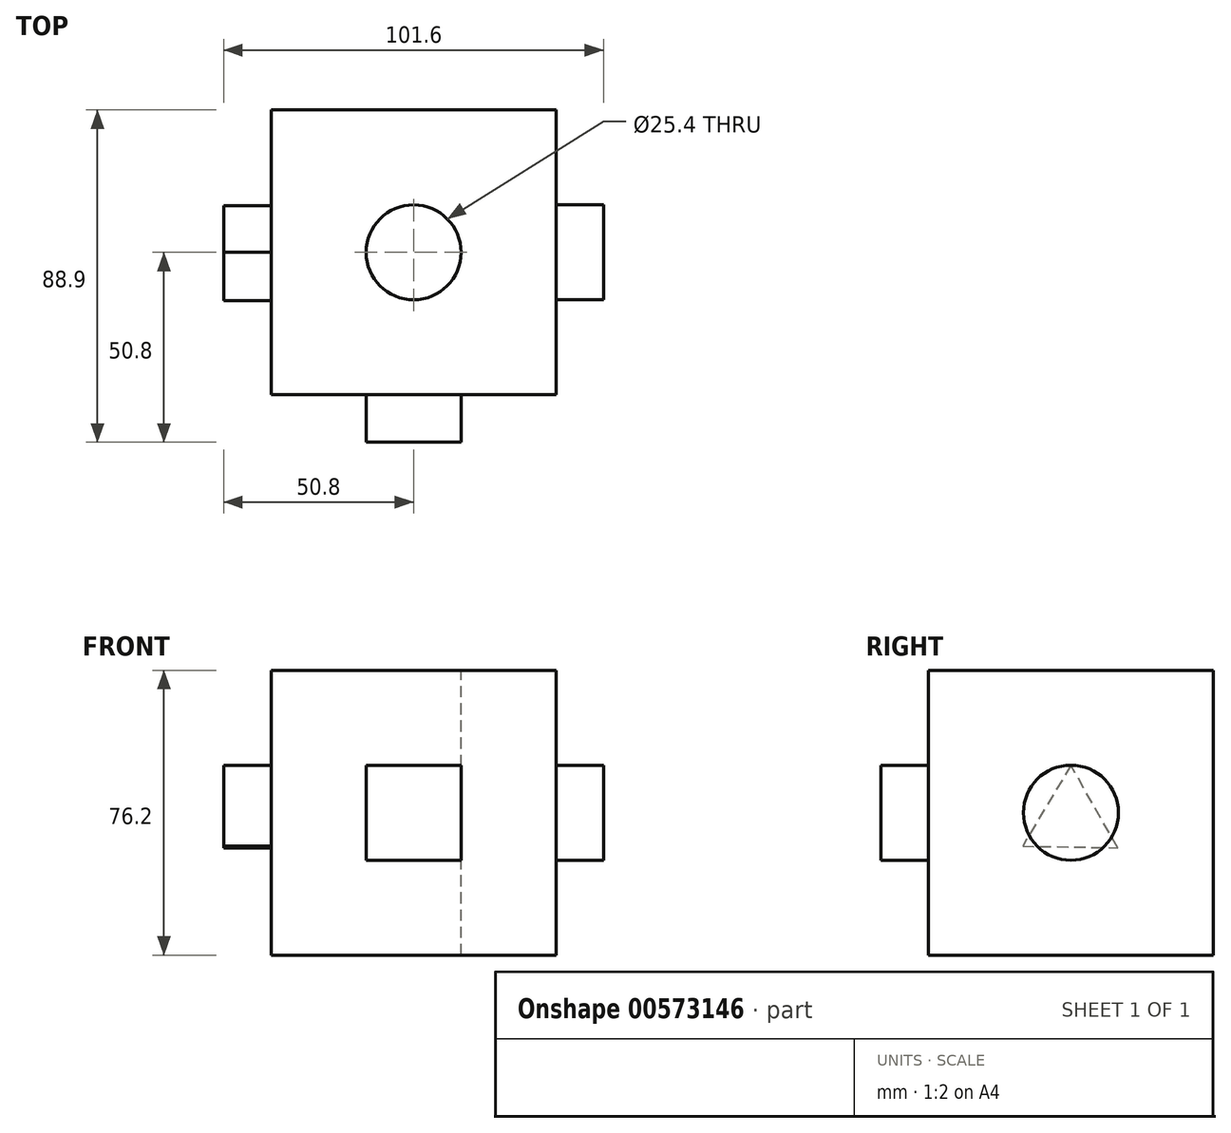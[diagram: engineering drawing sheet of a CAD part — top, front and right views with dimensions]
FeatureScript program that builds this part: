
annotation { "Feature Type Name" : "Feature", "Feature Type Description" : "" }
export const myFeature = defineFeature(function(context is Context, id is Id, definition is map)
    precondition{}
    {
        {
            var Q0;
            Q0=qCreatedBy(makeId("Front.planeOp"),FACE);
            var sketch = newSketch(context, id + "F0", { "sketchPlane" : qUnion([Q0])});
            skLineSegment(sketch, "E0.bottom", {"start": v(0, 0) * mm, "end": v(-76.2, 0) * mm});
            skLineSegment(sketch, "E0.top", {"start": v(0, 76.2) * mm, "end": v(-76.2, 76.2) * mm});
            skLineSegment(sketch, "E0.left", {"start": v(0, 0) * mm, "end": v(0, 76.2) * mm});
            skLineSegment(sketch, "E0.right", {"start": v(-76.2, 0) * mm, "end": v(-76.2, 76.2) * mm});
            skSolve(sketch);
        }
        {
            var Q0;
            Q0=makeQuery(id+"F0.imprint","IMPRINT",FACE,{"disambiguationData":[TD([[makeQuery(id+"F0.imprint","IMPRINT",EDGE,{"derivedFrom":sQuery(id+"F0.wireOp",EDGE,"E0.bottom")}),-1.0]])]});
            extrude(context, id + "F1", {"entities" : qUnion([Q0]), "depth" : 76.2 * mm, "offsetDistance" : 25.4 * mm});
        }
        {
            var Q0;
            Q0=makeQuery(id+"F1.opExtrude","CAP_FACE",FACE,{"disambiguationData":[OSD([sQuery(id+"F0.wireOp",EDGE,"E0.bottom"),sQuery(id+"F0.wireOp",EDGE,"E0.top"),sQuery(id+"F0.wireOp",EDGE,"E0.left"),sQuery(id+"F0.wireOp",EDGE,"E0.right")])],"isStart":false});
            var sketch = newSketch(context, id + "F2", { "sketchPlane" : qUnion([Q0])});
            skLineSegment(sketch, "E1.bottom", {"start": v(-50.8, 50.8) * mm, "end": v(-25.4, 50.8) * mm});
            skLineSegment(sketch, "E1.top", {"start": v(-50.8, 25.4) * mm, "end": v(-25.4, 25.4) * mm});
            skLineSegment(sketch, "E1.left", {"start": v(-50.8, 50.8) * mm, "end": v(-50.8, 25.4) * mm});
            skLineSegment(sketch, "E1.right", {"start": v(-25.4, 50.8) * mm, "end": v(-25.4, 25.4) * mm});
            skSolve(sketch);
        }
        {
            var Q0;
            Q0=makeQuery(id+"F2.imprint","IMPRINT",FACE,{"disambiguationData":[TD([[makeQuery(id+"F2.imprint","IMPRINT",EDGE,{"derivedFrom":sQuery(id+"F2.wireOp",EDGE,"E1.bottom")}),-1.0]])]});
            extrude(context, id + "F3", {"entities" : qUnion([Q0]), "operationType" : NewBodyOperationType.ADD, "depth" : 12.7 * mm, "offsetDistance" : 25.4 * mm});
        }
        {
            var Q0;
            Q0=makeQuery(id+"F1.opExtrude","SWEPT_FACE",FACE,{"disambiguationData":[OSD([sQuery(id+"F0.wireOp",EDGE,"E0.left")])]});
            var sketch = newSketch(context, id + "F4", { "sketchPlane" : qUnion([Q0])});
            skCircle(sketch, "E2", {"center": v(-38.1, 38.1) * mm, "radius": 12.7 * mm});
            skSolve(sketch);
        }
        {
            var Q0;
            Q0=makeQuery(id+"F4.imprint","IMPRINT",FACE,{"disambiguationData":[TD([[makeQuery(id+"F4.imprint","IMPRINT",EDGE,{"derivedFrom":sQuery(id+"F4.wireOp",EDGE,"E2")}),1.0]])]});
            extrude(context, id + "F5", {"entities" : qUnion([Q0]), "operationType" : NewBodyOperationType.ADD, "depth" : 12.7 * mm, "offsetDistance" : 25.4 * mm});
        }
        {
            var Q0;
            Q0=makeQuery(id+"F1.opExtrude","SWEPT_FACE",FACE,{"disambiguationData":[OSD([sQuery(id+"F0.wireOp",EDGE,"E0.top")])]});
            var sketch = newSketch(context, id + "F6", { "sketchPlane" : qUnion([Q0])});
            skPoint(sketch, "E3", {"position": v(-38.1, -38.1) * mm});
            skSolve(sketch);
        }
        {
            var Q0;
            {var subQ0=sQuery(id+"F0.wireOp",EDGE,"E0.top");Q0=makeQuery(id+"F6.imprint","IMPRINT",FACE,{"disambiguationData":[TD([[makeQuery(id+"F6.imprint","IMPRINT",EDGE,{"derivedFrom":makeQuery(id+"F1.opExtrude","CAP_EDGE",EDGE,{"disambiguationData":[OSD([subQ0])],"isStart":true})}),1.0]])]});}
            var sketch = newSketch(context, id + "F7", { "sketchPlane" : qUnion([Q0])});
            skCircle(sketch, "E4", {"center": v(-38.1, -38.1) * mm, "radius": 12.7 * mm});
            skSolve(sketch);
        }
        {
            var Q0;
            Q0=sQuery(id+"F6.wireOp",VERTEX,"E3");
            var Q1;
            Q1=makeQuery(id+"F1.opExtrude","SWEPT_BODY",BODY,{"disambiguationData":[OSD([sQuery(id+"F0.wireOp",EDGE,"E0.bottom"),sQuery(id+"F0.wireOp",EDGE,"E0.top"),sQuery(id+"F0.wireOp",EDGE,"E0.left"),sQuery(id+"F0.wireOp",EDGE,"E0.right")])]});
            hole(context, id + "F8", {"style" : HoleStyle.SIMPLE, "endStyle" : HoleEndStyle.THROUGH, "holeDiameter" : 25.4 * mm, "isTappedThrough" : true, "tappedDepth" : 12.7 * mm, "tapClearance" : 3, "locations" : qUnion([Q0]), "scope" : qUnion([Q1])});
        }
        {
            var Q0;
            Q0=makeQuery(id+"F1.opExtrude","SWEPT_FACE",FACE,{"disambiguationData":[OSD([sQuery(id+"F0.wireOp",EDGE,"E0.right")])]});
            var sketch = newSketch(context, id + "F9", { "sketchPlane" : qUnion([Q0])});
            skLineSegment(sketch, "E5", {"start": v(25.6, 28.7) * mm, "end": v(38.1, 50.8) * mm});
            skLineSegment(sketch, "E6", {"start": v(38.1, 50.8) * mm, "end": v(50.99, 29.14) * mm});
            skLineSegment(sketch, "E7", {"start": v(50.99, 29.14) * mm, "end": v(25.6, 28.7) * mm});
            skSolve(sketch);
        }
        {
            var Q0;
            Q0=makeQuery(id+"F9.imprint","IMPRINT",FACE,{"disambiguationData":[TD([[makeQuery(id+"F9.imprint","IMPRINT",EDGE,{"derivedFrom":sQuery(id+"F9.wireOp",EDGE,"E5")}),-1.0]])]});
            extrude(context, id + "F10", {"entities" : qUnion([Q0]), "operationType" : NewBodyOperationType.ADD, "depth" : 12.7 * mm, "offsetDistance" : 25.4 * mm});
        }
    });
